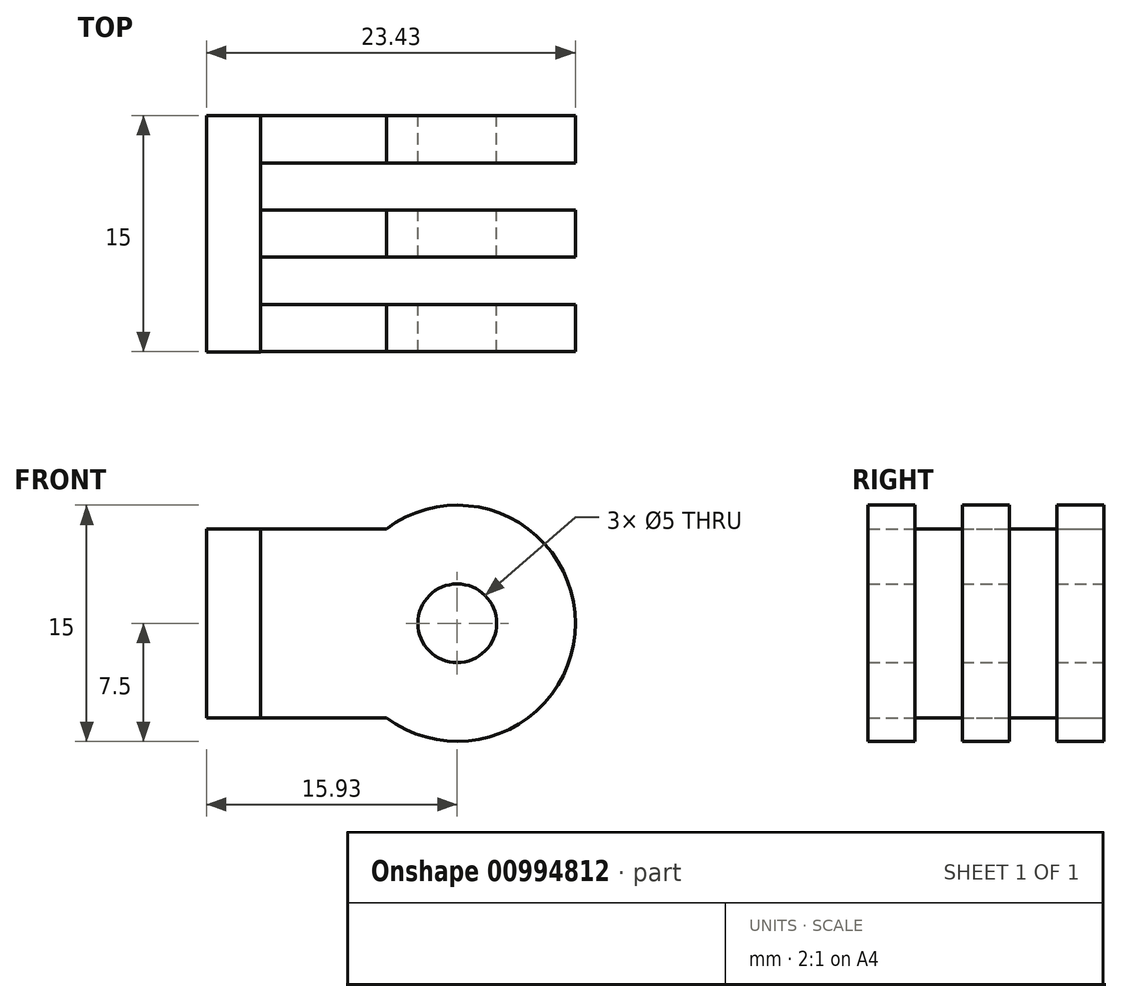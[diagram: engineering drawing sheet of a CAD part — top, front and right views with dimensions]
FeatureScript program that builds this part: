
annotation { "Feature Type Name" : "Feature", "Feature Type Description" : "" }
export const myFeature = defineFeature(function(context is Context, id is Id, definition is map)
    precondition{}
    {
        {
            var Q0;
            Q0=qCreatedBy(makeId("Front.planeOp"),FACE);
            var sketch = newSketch(context, id + "F0", { "sketchPlane" : qUnion([Q0])});
            skCircle(sketch, "E0", {"center": v(0, 0) * mm, "radius": 7.5 * mm});
            skCircle(sketch, "E1", {"center": v(0, 0) * mm, "radius": 2.5 * mm});
            skLineSegment(sketch, "E2.bottom", {"start": v(-4.5, -6) * mm, "end": v(4.5, -6) * mm});
            skLineSegment(sketch, "E2.left", {"start": v(-4.5, -6) * mm, "end": v(-4.5, 6) * mm});
            skLineSegment(sketch, "E2.right", {"start": v(4.5, -6) * mm, "end": v(4.5, 6) * mm});
            skLineSegment(sketch, "E3", {"start": v(-4.5, -6) * mm, "end": v(-12.5, -6) * mm});
            skLineSegment(sketch, "E4", {"start": v(-12.5, -6) * mm, "end": v(-12.5, 6) * mm});
            skLineSegment(sketch, "E5", {"start": v(4.5, 6) * mm, "end": v(-12.5, 6) * mm});
            skSolve(sketch);
        }
        {
            var Q0;
            Q0=qSketchRegion(id+"F0",true);
            extrude(context, id + "F1", {"entities" : qUnion([Q0]), "endBound" : BoundingType.SYMMETRIC, "depth" : 3 * mm, "offsetDistance" : 25.4 * mm});
        }
        {
            var Q0;
            Q0=qSketchRegion(id+"F0",true);
            extrude(context, id + "F2", {"entities" : qUnion([Q0]), "oppositeDirection" : true, "depth" : 3 * mm, "offsetDistance" : 25.4 * mm});
        }
        {
            var Q0;
            Q0=makeQuery(id+"F2.opExtrude","SWEPT_BODY",BODY,{"disambiguationData":[OSD([sQuery(id+"F0.wireOp",EDGE,"E0"),sQuery(id+"F0.wireOp",EDGE,"E1"),sQuery(id+"F0.wireOp",EDGE,"E3"),sQuery(id+"F0.wireOp",EDGE,"E4"),sQuery(id+"F0.wireOp",EDGE,"E5")])]});
            transform(context, id + "F3", {"entities" : qUnion([Q0]), "transformType" : TransformType.TRANSLATION_3D, "dx" : 0 * mm, "dy" : 1.5 * mm, "dz" : 0 * mm, "makeCopy" : false});
        }
        {
            var Q0;
            Q0=qSketchRegion(id+"F0",true);
            extrude(context, id + "F4", {"entities" : qUnion([Q0]), "depth" : 3 * mm, "offsetDistance" : 25.4 * mm});
        }
        {
            var Q0;
            Q0=makeQuery(id+"F4.opExtrude","SWEPT_BODY",BODY,{"disambiguationData":[OSD([sQuery(id+"F0.wireOp",EDGE,"E0"),sQuery(id+"F0.wireOp",EDGE,"E1"),sQuery(id+"F0.wireOp",EDGE,"E3"),sQuery(id+"F0.wireOp",EDGE,"E4"),sQuery(id+"F0.wireOp",EDGE,"E5")])]});
            transform(context, id + "F5", {"entities" : qUnion([Q0]), "transformType" : TransformType.TRANSLATION_3D, "dx" : 0 * mm, "dy" : -1.5 * mm, "dz" : 0 * mm, "makeCopy" : false});
        }
        {
            var Q0;
            Q0=qSketchRegion(id+"F0",true);
            extrude(context, id + "F6", {"entities" : qUnion([Q0]), "depth" : 3 * mm, "offsetDistance" : 25.4 * mm});
        }
        {
            var Q0;
            Q0=makeQuery(id+"F6.opExtrude","SWEPT_BODY",BODY,{"disambiguationData":[OSD([sQuery(id+"F0.wireOp",EDGE,"E0"),sQuery(id+"F0.wireOp",EDGE,"E1"),sQuery(id+"F0.wireOp",EDGE,"E3"),sQuery(id+"F0.wireOp",EDGE,"E4"),sQuery(id+"F0.wireOp",EDGE,"E5")])]});
            transform(context, id + "F7", {"entities" : qUnion([Q0]), "transformType" : TransformType.TRANSLATION_3D, "dx" : 0 * mm, "dy" : -4.5 * mm, "dz" : 0 * mm, "makeCopy" : false});
        }
        {
            var Q0;
            Q0=qSketchRegion(id+"F0",true);
            extrude(context, id + "F8", {"entities" : qUnion([Q0]), "depth" : 3 * mm, "offsetDistance" : 25.4 * mm});
        }
        {
            var Q0;
            Q0=makeQuery(id+"F8.opExtrude","SWEPT_BODY",BODY,{"disambiguationData":[OSD([sQuery(id+"F0.wireOp",EDGE,"E0"),sQuery(id+"F0.wireOp",EDGE,"E1"),sQuery(id+"F0.wireOp",EDGE,"E3"),sQuery(id+"F0.wireOp",EDGE,"E4"),sQuery(id+"F0.wireOp",EDGE,"E5")])]});
            transform(context, id + "F9", {"entities" : qUnion([Q0]), "transformType" : TransformType.TRANSLATION_3D, "dx" : 0 * mm, "dy" : 7.5 * mm, "dz" : 0 * mm, "makeCopy" : false});
        }
        {
            var Q0;
            Q0=qCreatedBy(makeId("Front.planeOp"),FACE);
            var sketch = newSketch(context, id + "F10", { "sketchPlane" : qUnion([Q0])});
            skPoint(sketch, "E6.middle", {"position": v(0, 0) * mm});
            skLineSegment(sketch, "E7", {"start": v(-15.96, -6) * mm, "end": v(-15.96, 6) * mm});
            skLineSegment(sketch, "E8", {"start": v(-12.5, 6) * mm, "end": v(-12.5, -6) * mm});
            skLineSegment(sketch, "E9", {"start": v(-15.96, -6) * mm, "end": v(-12.5, -6) * mm});
            skLineSegment(sketch, "E10", {"start": v(-15.96, 6) * mm, "end": v(-12.5, 6) * mm});
            skSolve(sketch);
        }
        {
            var Q0;
            Q0=qSketchRegion(id+"F10",true);
            extrude(context, id + "F11", {"entities" : qUnion([Q0]), "endBound" : BoundingType.SYMMETRIC, "depth" : 15 * mm, "offsetDistance" : 25.4 * mm});
        }
        {
            var Q0;
            Q0=makeQuery(id+"F11.opExtrude","SWEPT_BODY",BODY,{"disambiguationData":[OSD([sQuery(id+"F10.wireOp",EDGE,"E7"),sQuery(id+"F10.wireOp",EDGE,"E8"),sQuery(id+"F10.wireOp",EDGE,"E9"),sQuery(id+"F10.wireOp",EDGE,"E10")])]});
            transform(context, id + "F12", {"entities" : qUnion([Q0]), "transformType" : TransformType.TRANSLATION_3D, "dx" : 0.03 * mm, "dy" : 0 * mm, "dz" : 0 * mm, "makeCopy" : false});
        }
        {
            var Q0;
            Q0=makeQuery(id+"F4.opExtrude","SWEPT_BODY",BODY,{"disambiguationData":[OSD([sQuery(id+"F0.wireOp",EDGE,"E0"),sQuery(id+"F0.wireOp",EDGE,"E1"),sQuery(id+"F0.wireOp",EDGE,"E3"),sQuery(id+"F0.wireOp",EDGE,"E4"),sQuery(id+"F0.wireOp",EDGE,"E5")])]});
            deleteBodies(context, id + "F13", {"entities" : qUnion([Q0])});
        }
        {
            var Q0;
            Q0=makeQuery(id+"F2.opExtrude","SWEPT_BODY",BODY,{"disambiguationData":[OSD([sQuery(id+"F0.wireOp",EDGE,"E0"),sQuery(id+"F0.wireOp",EDGE,"E1"),sQuery(id+"F0.wireOp",EDGE,"E3"),sQuery(id+"F0.wireOp",EDGE,"E4"),sQuery(id+"F0.wireOp",EDGE,"E5")])]});
            deleteBodies(context, id + "F14", {"entities" : qUnion([Q0])});
        }
    });
